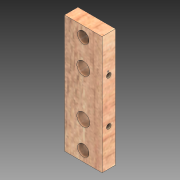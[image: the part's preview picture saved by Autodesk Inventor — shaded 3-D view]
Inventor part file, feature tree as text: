
AUTODESK INVENTOR PART (.ipt)
format: ipt  version: 2020 (Build 240168000, 168)  size: 145,408 bytes
history: native  units: mm
features: extrude x2, sketch x2
ambient origin geometry x8: Origin, YZ Plane, XZ Plane, XY Plane, X Axis, Y Axis, Z Axis, Center Point
bodies: Solid1 (feature_tree)
feature tree (4):
  extrude  "Extrusion1"  Depth=9.6mm
  extrude  "Extrusion2"  Depth=16.5mm
  sketch  "Sketch1"  dims[d0=28.0mm d2=9.6mm]
  sketch  "Sketch2"  dims[d3=9.6mm d8=8.5mm d9=8.5mm d11=20.0mm d12=20.0mm d17=10.0mm d18=0.0mm d23=3.45mm d24=3.45mm d25=16.5mm d26=16.5mm d27=5.0mm d28=5.0mm d29=15.0mm d30=0.0mm d37=44.0mm d38=44.0mm d45=33.0mm]
